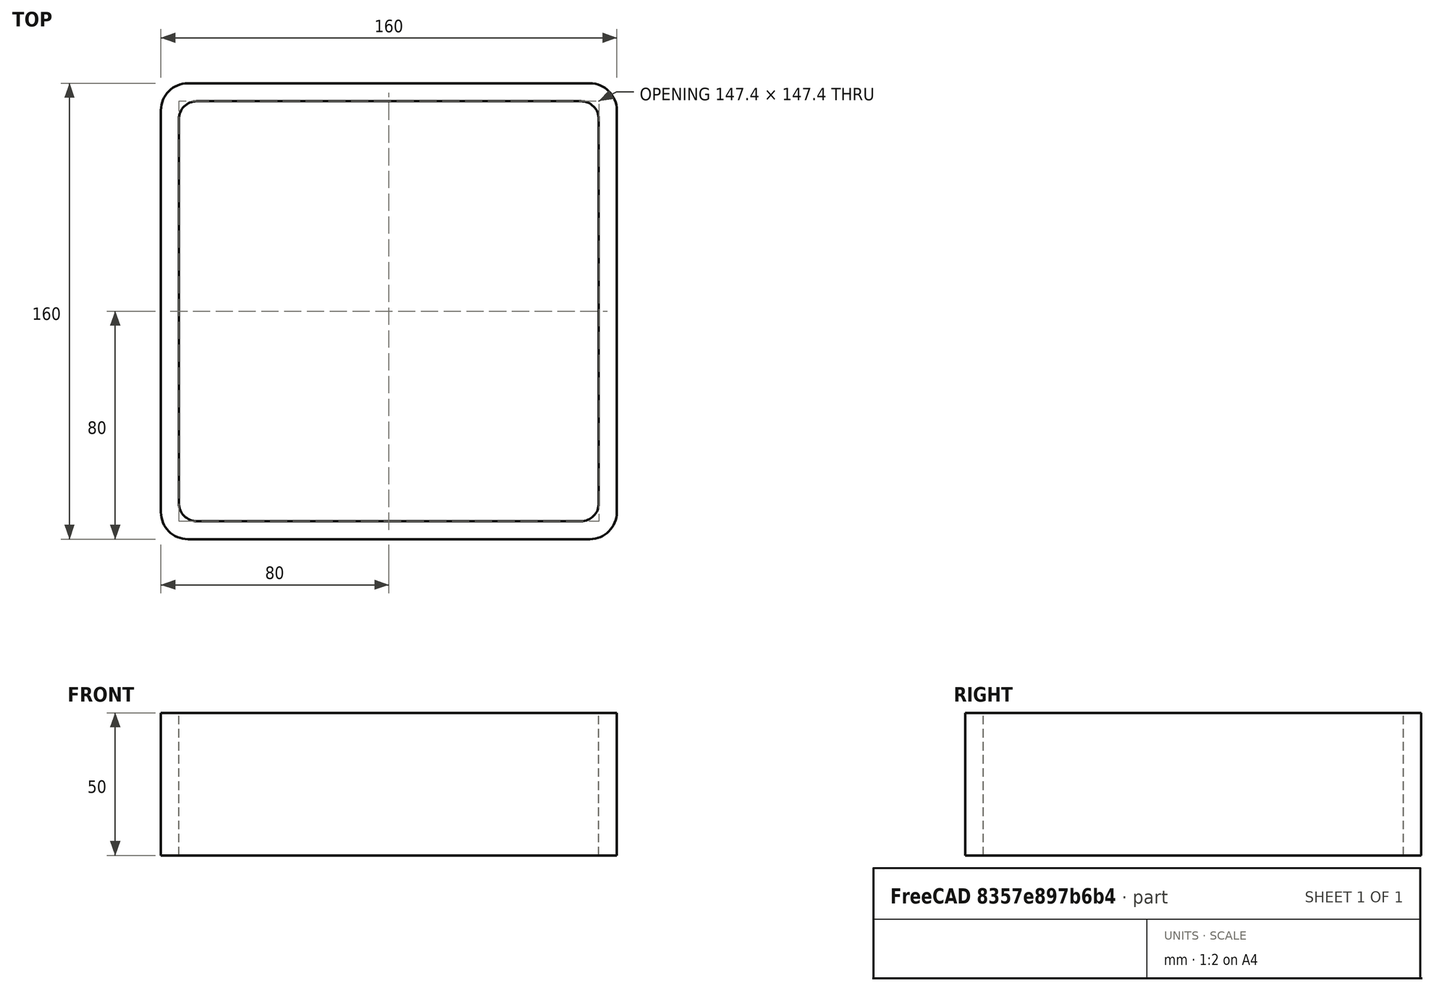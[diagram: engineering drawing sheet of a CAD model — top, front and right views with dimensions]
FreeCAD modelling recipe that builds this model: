
FCSTD DOCUMENT  (FreeCAD 0.15R4671 (Git))
Label: Square hollow section 160x160x6.3 EN10219 S235JRH
License: All rights reserved
LicenseURL: http://en.wikipedia.org/wiki/All_rights_reserved
objects: Sketcher::SketchObject×1, Part::Extrusion×1
note: 2 computed .brp shape members not serialized (recipe doc carries the construction recipe); baked Part::Feature solids carry a one-line shape summary decoded from their .brp

FEATURE [Sketcher::SketchObject] Sketch
  sketch-geometry (16):
    g0: LineSegment StartX=-67.4 StartY=73.7 StartZ=0 EndX=67.4 EndY=73.7 EndZ=0
    g1: LineSegment StartX=73.7 StartY=67.4 StartZ=0 EndX=73.7 EndY=-67.4 EndZ=0
    g2: LineSegment StartX=67.4 StartY=-73.7 StartZ=0 EndX=-67.4 EndY=-73.7 EndZ=0
    g3: LineSegment StartX=-73.7 StartY=-67.4 StartZ=0 EndX=-73.7 EndY=67.4 EndZ=0
    g4: LineSegment StartX=-70.55 StartY=80 StartZ=0 EndX=70.55 EndY=80 EndZ=0
    g5: LineSegment StartX=80 StartY=70.55 StartZ=0 EndX=80 EndY=-70.55 EndZ=0
    g6: LineSegment StartX=70.55 StartY=-80 StartZ=0 EndX=-70.55 EndY=-80 EndZ=0
    g7: LineSegment StartX=-80 StartY=-70.55 StartZ=0 EndX=-80 EndY=70.55 EndZ=0
    g8: ArcOfCircle CenterX=-67.4 CenterY=67.4 CenterZ=0 NormalX=0 NormalY=0 NormalZ=1 Radius=6.3 StartAngle=1.5708 EndAngle=3.14159
    g9: ArcOfCircle CenterX=67.4 CenterY=67.4 CenterZ=0 NormalX=0 NormalY=0 NormalZ=1 Radius=6.3 StartAngle=0 EndAngle=1.5708
    g10: ArcOfCircle CenterX=67.4 CenterY=-67.4 CenterZ=0 NormalX=0 NormalY=0 NormalZ=1 Radius=6.3 StartAngle=4.71239 EndAngle=6.28319
    g11: ArcOfCircle CenterX=-67.4 CenterY=-67.4 CenterZ=0 NormalX=0 NormalY=0 NormalZ=1 Radius=6.3 StartAngle=3.14159 EndAngle=4.71239
    g12: ArcOfCircle CenterX=70.55 CenterY=70.55 CenterZ=0 NormalX=0 NormalY=0 NormalZ=1 Radius=9.45 StartAngle=0 EndAngle=1.5708
    g13: ArcOfCircle CenterX=70.55 CenterY=-70.55 CenterZ=0 NormalX=0 NormalY=0 NormalZ=1 Radius=9.45 StartAngle=4.71239 EndAngle=6.28319
    g14: ArcOfCircle CenterX=-70.55 CenterY=-70.55 CenterZ=0 NormalX=0 NormalY=0 NormalZ=1 Radius=9.45 StartAngle=3.14159 EndAngle=4.71239
    g15: ArcOfCircle CenterX=-70.55 CenterY=70.55 CenterZ=0 NormalX=0 NormalY=0 NormalZ=1 Radius=9.45 StartAngle=1.5708 EndAngle=3.14159
  constraints (36):
    c: Horizontal(g2)
    c: Vertical(g3)
    c: Horizontal(g6)
    c: Vertical(g7)
    c: Tangent(g3,g8) = 1.5708
    c: Tangent(g0,g8) = 1.5708
    c: Tangent(g0,g9) = 1.5708
    c: Tangent(g1,g9) = 1.5708
    c: Tangent(g1,g10) = 1.5708
    c: Tangent(g2,g10) = 1.5708
    c: Tangent(g2,g11) = 1.5708
    c: Tangent(g3,g11) = 1.5708
    c: Tangent(g4,g12) = 1.5708
    c: Tangent(g5,g12) = 1.5708
    c: Tangent(g5,g13) = 1.5708
    c: Tangent(g6,g13) = 1.5708
    c: Tangent(g6,g14) = 1.5708
    c: Tangent(g7,g14) = 1.5708
    c: Tangent(g7,g15) = 1.5708
    c: Tangent(g4,g15) = 1.5708
    c: Equal(g9,g8)
    c: Equal(g9,g11)
    c: Equal(g9,g10)
    c: Equal(g12,g15)
    c: Equal(g12,g14)
    c: Equal(g12,g13)
    c: Symmetric(g4,g6,g-1)
    c: Symmetric(g7,g5,g-2)
    c: DistanceY(g4,g6) = -160
    c: DistanceX(g7,g5) = 160
    c: Symmetric(g3,g1,g-2)
    c: Symmetric(g0,g2,g-1)
    c: DistanceY(g0,g4) = 6.3
    c: DistanceX(g5,g1) = -6.3
    c: Radius(g9) = 6.3
    c: Radius(g12) = 9.45
FEATURE [Part::Extrusion] Extrude  label="Square hollow section 160x160x6.3 EN10219 S235JRH"
  Base = -> Sketch
  Dir = (0,0,50)
  Solid = true
